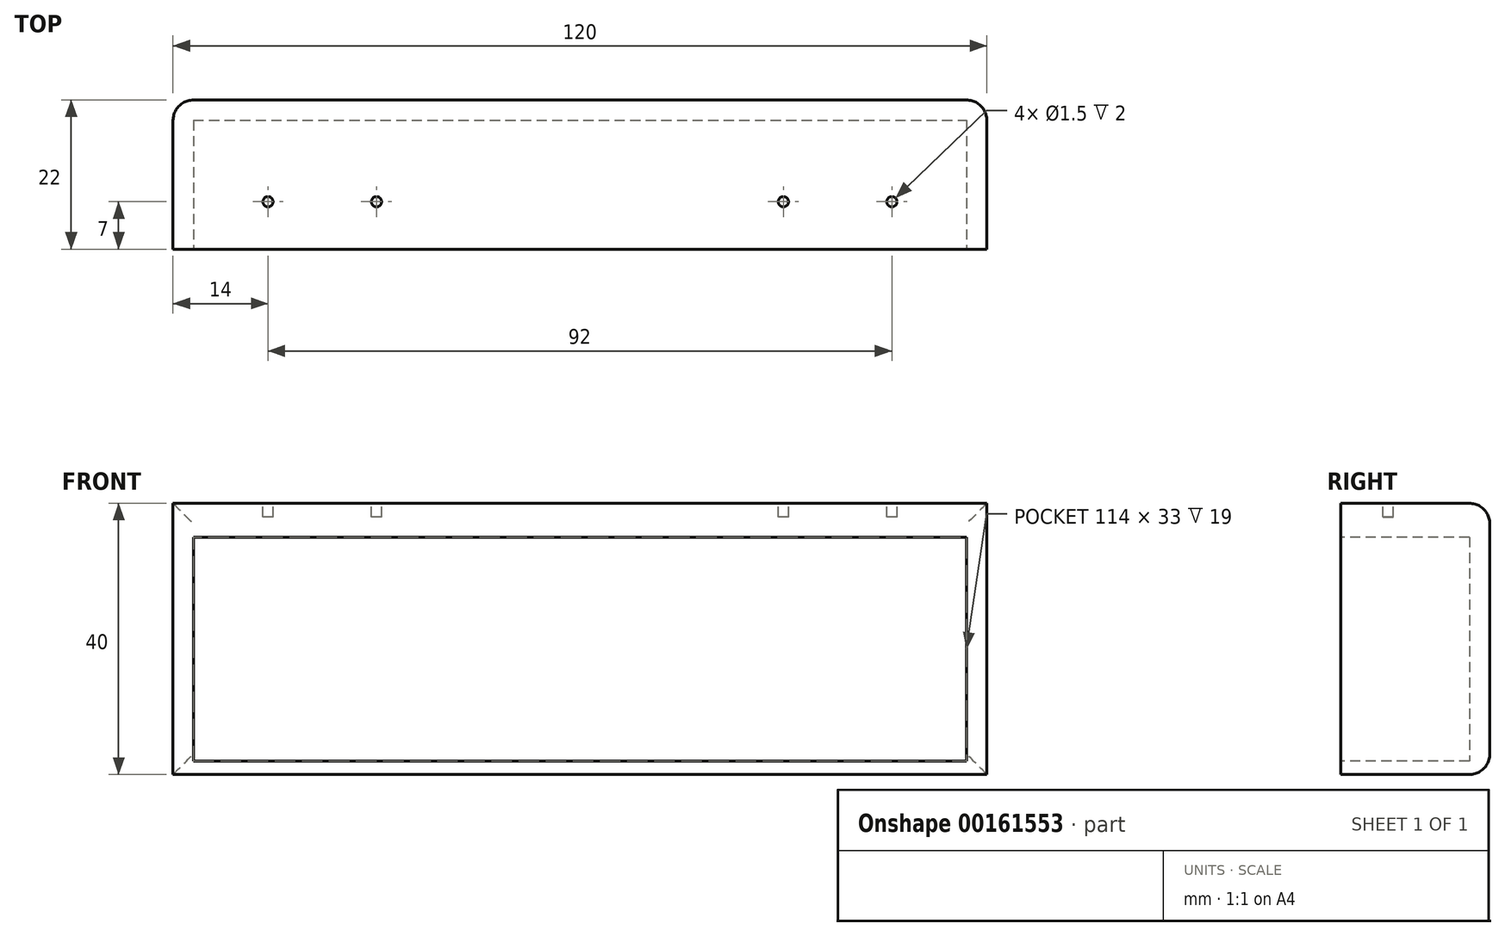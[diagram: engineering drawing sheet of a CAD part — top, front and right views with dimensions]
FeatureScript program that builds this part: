
annotation { "Feature Type Name" : "Feature", "Feature Type Description" : "" }
export const myFeature = defineFeature(function(context is Context, id is Id, definition is map)
    precondition{}
    {
        {
            var Q0;
            Q0=qCreatedBy(makeId("Front.planeOp"),FACE);
            var sketch = newSketch(context, id + "F0", { "sketchPlane" : qUnion([Q0])});
            skLineSegment(sketch, "E0.bottom", {"start": v(-60, 20) * mm, "end": v(60, 20) * mm});
            skLineSegment(sketch, "E0.top", {"start": v(-60, -20) * mm, "end": v(60, -20) * mm});
            skLineSegment(sketch, "E0.left", {"start": v(-60, 20) * mm, "end": v(-60, -20) * mm});
            skLineSegment(sketch, "E0.right", {"start": v(60, 20) * mm, "end": v(60, -20) * mm});
            skPoint(sketch, "E0.middle", {"position": v(0, 0) * mm});
            skSolve(sketch);
        }
        {
            var Q0;
            Q0=makeQuery(id+"F0.imprint","IMPRINT",FACE,{"disambiguationData":[TD([[makeQuery(id+"F0.imprint","IMPRINT",EDGE,{"derivedFrom":sQuery(id+"F0.wireOp",EDGE,"E0.bottom")}),-1.0]])]});
            extrude(context, id + "F1", {"entities" : qUnion([Q0]), "depth" : 22 * mm});
        }
        {
            var Q0;
            Q0=makeQuery(id+"F1.opExtrude","CAP_FACE",FACE,{"disambiguationData":[OSD([sQuery(id+"F0.wireOp",EDGE,"E0.bottom"),sQuery(id+"F0.wireOp",EDGE,"E0.top"),sQuery(id+"F0.wireOp",EDGE,"E0.left"),sQuery(id+"F0.wireOp",EDGE,"E0.right")])],"isStart":false});
            var sketch = newSketch(context, id + "F2", { "sketchPlane" : qUnion([Q0])});
            skPoint(sketch, "E1.middle", {"position": v(0, 0) * mm});
            skLineSegment(sketch, "E2.top", {"start": v(-57, -18) * mm, "end": v(57, -18) * mm});
            skLineSegment(sketch, "E2.left", {"start": v(-57, 15) * mm, "end": v(-57, -18) * mm});
            skLineSegment(sketch, "E2.right", {"start": v(57, 15) * mm, "end": v(57, -18) * mm});
            skLineSegment(sketch, "E3", {"start": v(-57, 15) * mm, "end": v(57, 15) * mm});
            skPoint(sketch, "E4.orphan", {"position": v(-57, 18) * mm});
            skPoint(sketch, "E5.orphan", {"position": v(57, 18) * mm});
            skSolve(sketch);
        }
        {
            var Q0;
            Q0 = qSketchRegion(id + "F2", true);
            extrude(context, id + "F3", {"entities" : qUnion([Q0]), "operationType" : NewBodyOperationType.REMOVE, "oppositeDirection" : true, "depth" : 19 * mm});
        }
        {
            var Q0;
            Q0=makeQuery(id+"F1.opExtrude","CAP_FACE",FACE,{"disambiguationData":[OSD([sQuery(id+"F0.wireOp",EDGE,"E0.bottom"),sQuery(id+"F0.wireOp",EDGE,"E0.top"),sQuery(id+"F0.wireOp",EDGE,"E0.left"),sQuery(id+"F0.wireOp",EDGE,"E0.right")])],"isStart":true});
            fillet(context, id + "F4", {"entities" : qUnion([Q0]), "radius" : 3 * mm, "tangentPropagation" : true, "allowEdgeOverflow" : false});
        }
        {
            var Q0;
            Q0=makeQuery(id+"F1.opExtrude","SWEPT_FACE",FACE,{"disambiguationData":[OSD([sQuery(id+"F0.wireOp",EDGE,"E0.bottom")])]});
            var sketch = newSketch(context, id + "F5", { "sketchPlane" : qUnion([Q0])});
            skPoint(sketch, "E6.end.orphan", {"position": v(-50, -19.76) * mm});
            skPoint(sketch, "E7.end.orphan", {"position": v(25, -19.76) * mm});
            skCircle(sketch, "E8", {"center": v(-46, -15) * mm, "radius": 0.75 * mm});
            skCircle(sketch, "E9", {"center": v(-30, -15) * mm, "radius": 0.75 * mm});
            skCircle(sketch, "E10", {"center": v(30, -15) * mm, "radius": 0.75 * mm});
            skCircle(sketch, "E11", {"center": v(46, -15) * mm, "radius": 0.75 * mm});
            skSolve(sketch);
        }
        {
            var Q0;
            Q0 = qSketchRegion(id + "F5", true);
            extrude(context, id + "F6", {"entities" : qUnion([Q0]), "operationType" : NewBodyOperationType.REMOVE, "oppositeDirection" : true, "depth" : 2 * mm});
        }
    });
